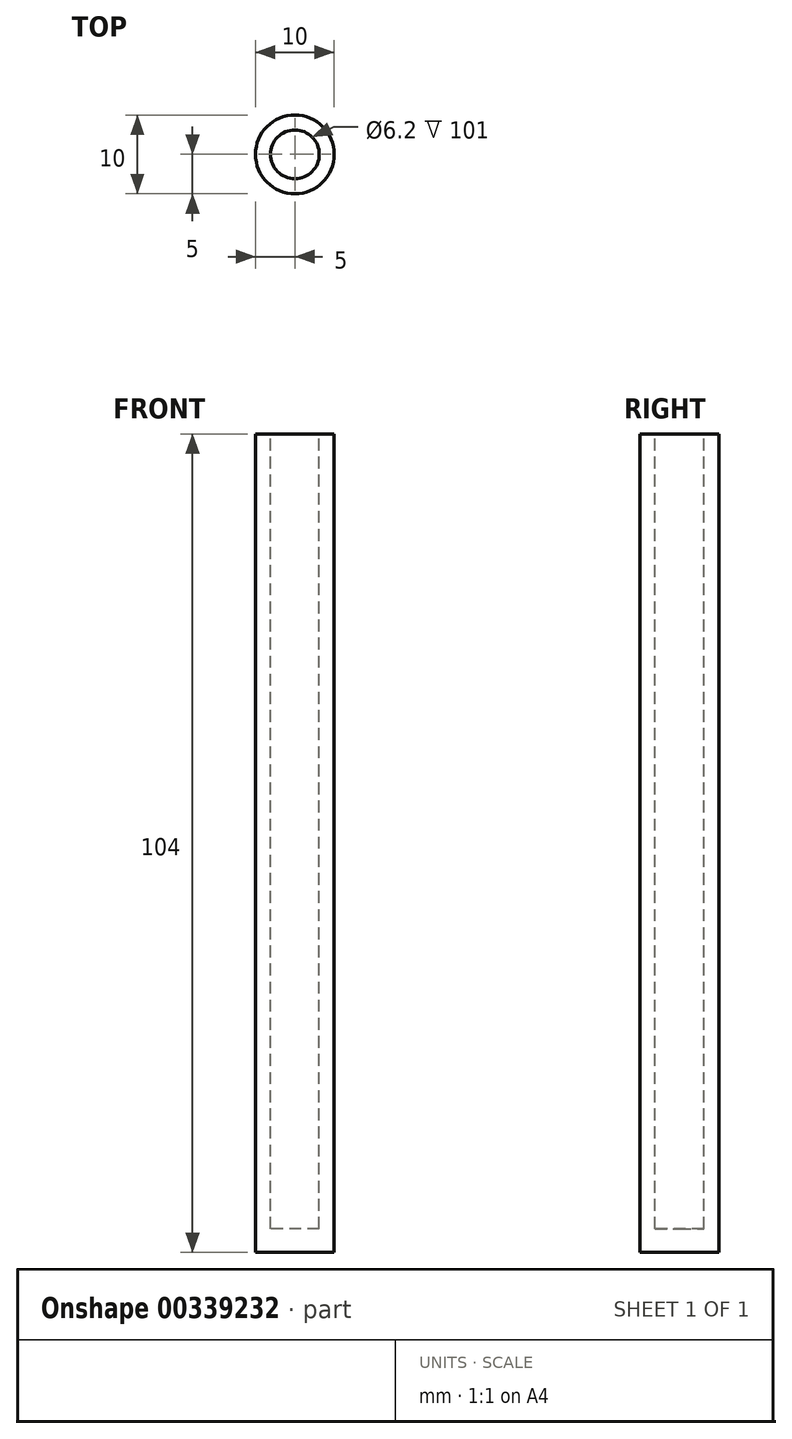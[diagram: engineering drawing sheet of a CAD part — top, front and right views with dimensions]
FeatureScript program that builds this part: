
annotation { "Feature Type Name" : "Feature", "Feature Type Description" : "" }
export const myFeature = defineFeature(function(context is Context, id is Id, definition is map)
    precondition{}
    {
        {
            var Q0;
            Q0=qCreatedBy(makeId("Top.planeOp"),FACE);
            var sketch = newSketch(context, id + "F0", { "sketchPlane" : qUnion([Q0])});
            skCircle(sketch, "E0", {"center": v(0, 0) * mm, "radius": 5 * mm});
            skSolve(sketch);
        }
        {
            var Q0;
            Q0=makeQuery(id+"F0.imprint","IMPRINT",FACE,{"disambiguationData":[TD([[makeQuery(id+"F0.imprint","IMPRINT",EDGE,{"derivedFrom":sQuery(id+"F0.wireOp",EDGE,"E0")}),1.0]])]});
            extrude(context, id + "F1", {"entities" : qUnion([Q0]), "depth" : (98 + 6) * mm});
        }
        {
            var Q0;
            Q0=makeQuery(id+"F1.opExtrude","CAP_FACE",FACE,{"disambiguationData":[OSD([sQuery(id+"F0.wireOp",EDGE,"E0")])],"isStart":false});
            var sketch = newSketch(context, id + "F2", { "sketchPlane" : qUnion([Q0])});
            skCircle(sketch, "E1.0.0", {"center": v(0, 0) * mm, "radius": 5 * mm});
            skCircle(sketch, "E2", {"center": v(0, 0) * mm, "radius": 3.1 * mm});
            skSolve(sketch);
        }
        {
            var Q0;
            Q0=makeQuery(id+"F2.imprint","IMPRINT",FACE,{"disambiguationData":[TD([[makeQuery(id+"F2.imprint","IMPRINT",EDGE,{"derivedFrom":sQuery(id+"F2.wireOp",EDGE,"E2")}),1.0]])]});
            extrude(context, id + "F3", {"entities" : qUnion([Q0]), "operationType" : NewBodyOperationType.REMOVE, "oppositeDirection" : true, "depth" : (95 + 6) * mm});
        }
    });
